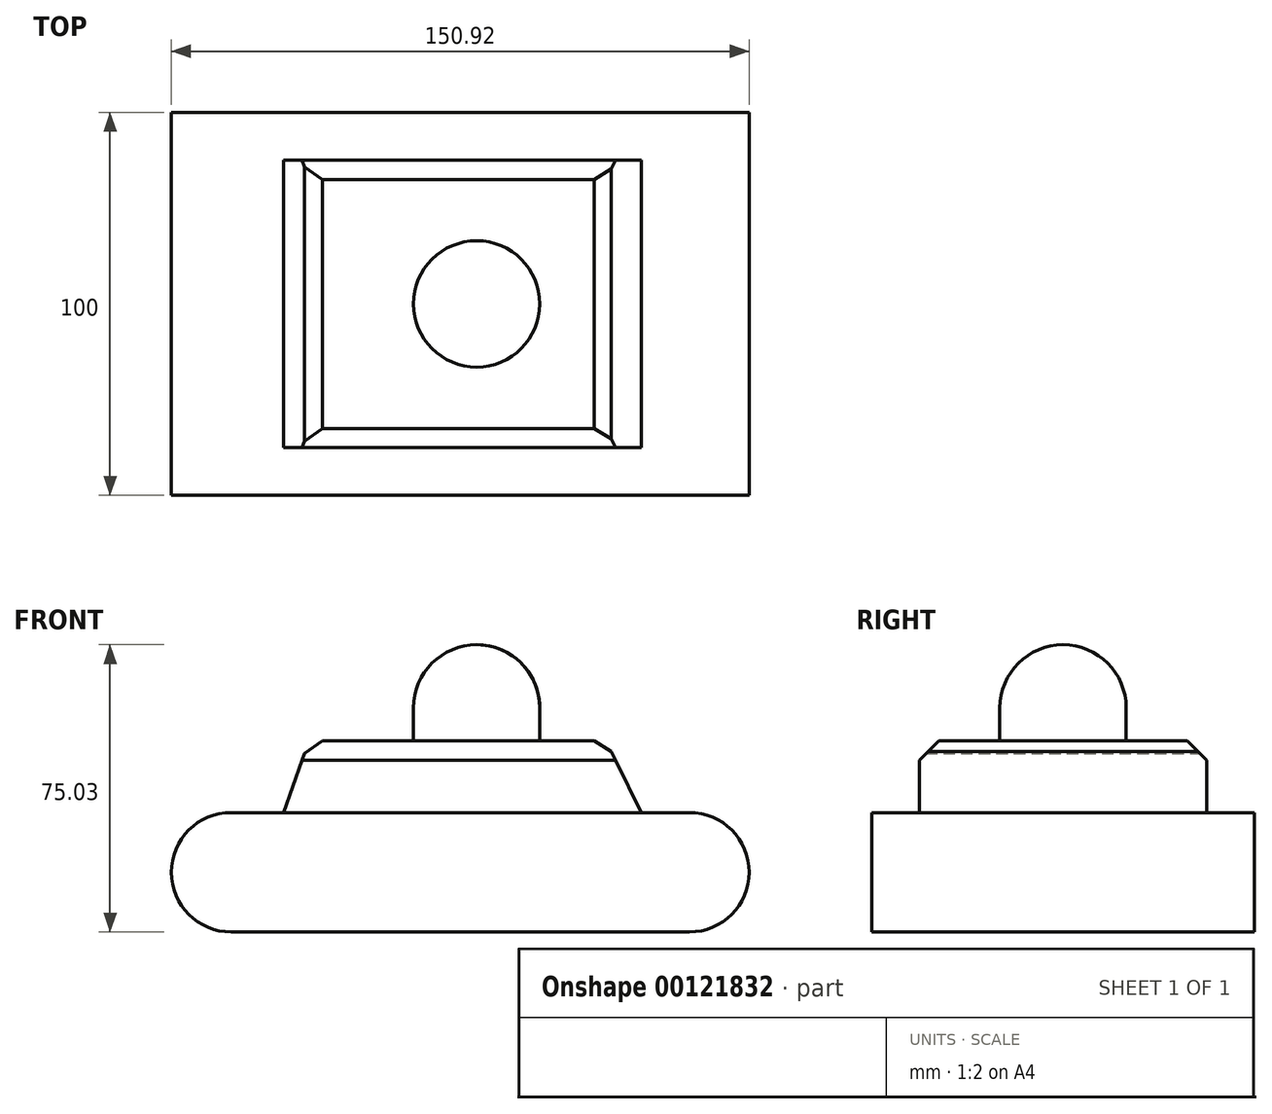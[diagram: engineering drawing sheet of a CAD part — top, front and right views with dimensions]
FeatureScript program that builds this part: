
annotation { "Feature Type Name" : "Feature", "Feature Type Description" : "" }
export const myFeature = defineFeature(function(context is Context, id is Id, definition is map)
    precondition{}
    {
        {
            var Q0;
            Q0=qCreatedBy(makeId("Front.planeOp"),FACE);
            var sketch = newSketch(context, id + "F0", { "sketchPlane" : qUnion([Q0])});
            skLineSegment(sketch, "E0.bottom", {"start": v(59.86, -15.6) * mm, "end": v(-59.86, -15.6) * mm});
            skLineSegment(sketch, "E0.top", {"start": v(59.86, 15.6) * mm, "end": v(-59.86, 15.6) * mm});
            skPoint(sketch, "E0.middle", {"position": v(0, 0) * mm});
            skArc(sketch, "E1", {"start": v(59.86, -15.6) * mm, "mid": v(75.46, 0) * mm, "end": v(59.86, 15.6) * mm});
            skArc(sketch, "E2", {"start": v(-59.86, 15.6) * mm, "mid": v(-75.46, 0) * mm, "end": v(-59.86, -15.6) * mm});
            skLineSegment(sketch, "E3", {"start": v(-46.2, 15.6) * mm, "end": v(-39.53, 34.3) * mm});
            skLineSegment(sketch, "E4", {"start": v(-39.53, 34.3) * mm, "end": v(38.06, 34.3) * mm});
            skLineSegment(sketch, "E5", {"start": v(38.06, 34.3) * mm, "end": v(47.3, 15.6) * mm});
            skLineSegment(sketch, "E6", {"start": v(-12.22, 34.3) * mm, "end": v(-12.22, 42.94) * mm});
            skLineSegment(sketch, "E7", {"start": v(20.78, 42.94) * mm, "end": v(20.78, 34.3) * mm});
            skArc(sketch, "E8", {"start": v(20.78, 42.94) * mm, "mid": v(4.28, 59.43) * mm, "end": v(-12.22, 42.94) * mm});
            skLineSegment(sketch, "E9", {"start": v(4.28, 42.94) * mm, "end": v(4.28, 59.43) * mm});
            skLineSegment(sketch, "E10", {"start": v(4.28, 42.94) * mm, "end": v(4.28, 34.3) * mm});
            skSolve(sketch);
        }
        {
            var Q0;
            Q0=makeQuery(id+"F0.imprint","IMPRINT",FACE,{"disambiguationData":[TD([[makeQuery(id+"F0.imprint","IMPRINT",EDGE,{"derivedFrom":sQuery(id+"F0.wireOp",EDGE,"E0.bottom")}),-1.0]])]});
            extrude(context, id + "F1", {"entities" : qUnion([Q0]), "endBound" : BoundingType.SYMMETRIC, "depth" : 100 * mm});
        }
        {
            var Q0;
            {var subQ3=sQuery(id+"F0.wireOp",EDGE,"E3");Q0=makeQuery(id+"F0.imprint","IMPRINT",FACE,{"disambiguationData":[TD([[makeQuery(id+"F0.imprint","IMPRINT",EDGE,{"derivedFrom":subQ3}),-1.0]])]});}
            extrude(context, id + "F2", {"entities" : qUnion([Q0]), "operationType" : NewBodyOperationType.ADD, "endBound" : BoundingType.SYMMETRIC, "depth" : 75 * mm});
        }
        {
            var Q0;
            {var subQ2=sQuery(id+"F0.wireOp",EDGE,"E7");Q0=makeQuery(id+"F0.imprint","IMPRINT",FACE,{"disambiguationData":[TD([[makeQuery(id+"F0.imprint","IMPRINT",EDGE,{"derivedFrom":subQ2}),-1.0]])]});}
            var Q1;
            Q1=sQuery(id+"F0.wireOp",EDGE,"E9");
            revolve(context, id + "F3", {"operationType" : NewBodyOperationType.ADD, "entities" : qUnion([Q0]), "axis" : qUnion([Q1]), "revolveType" : RevolveType.FULL});
        }
        {
            var Q0;
            Q0=makeQuery(id+"F2.opExtrude","CAP_EDGE",EDGE,{"disambiguationData":[OSD([sQuery(id+"F0.wireOp",EDGE,"E4")])],"isStart":false});
            var Q1;
            Q1=makeQuery(id+"F2.opExtrude","SWEPT_EDGE",EDGE,{"disambiguationData":[OSD([sQuery(id+"F0.wireOp",EDGE,"E4"),sQuery(id+"F0.wireOp",EDGE,"E5")])]});
            var Q2;
            Q2=makeQuery(id+"F2.opExtrude","CAP_EDGE",EDGE,{"disambiguationData":[OSD([sQuery(id+"F0.wireOp",EDGE,"E4")])],"isStart":true});
            var Q3;
            Q3=makeQuery(id+"F2.opExtrude","SWEPT_EDGE",EDGE,{"disambiguationData":[OSD([sQuery(id+"F0.wireOp",EDGE,"E3"),sQuery(id+"F0.wireOp",EDGE,"E4")])]});
            chamfer(context, id + "F4", {"entities" : qUnion([Q0, Q1, Q2, Q3]), "width" : 5 * mm, "tangentPropagation" : true});
        }
    });
